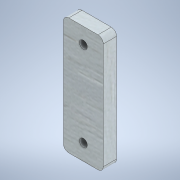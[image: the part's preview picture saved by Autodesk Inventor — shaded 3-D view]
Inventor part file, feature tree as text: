
AUTODESK INVENTOR PART (.ipt)
format: ipt  version: 2021 (Build 250183000, 183)  size: 125,440 bytes
history: native  units: mm
features: extrude x2, sketch x2
ambient origin geometry x8: Origin, YZ Plane, XZ Plane, XY Plane, X Axis, Y Axis, Z Axis, Center Point
bodies: Solid1 (feature_tree)
feature tree (4):
  extrude  "Extrusion1"  Depth=5.0mm
  extrude  "Extrusion2"  Depth=10.0mm
  sketch  "Sketch1"  dims[d0=5.0mm d1=0.0mm d2=3.0mm]
  sketch  "Sketch2"  dims[d3=7.5mm d4=3.0mm d5=10.0mm d6=0.0mm]
